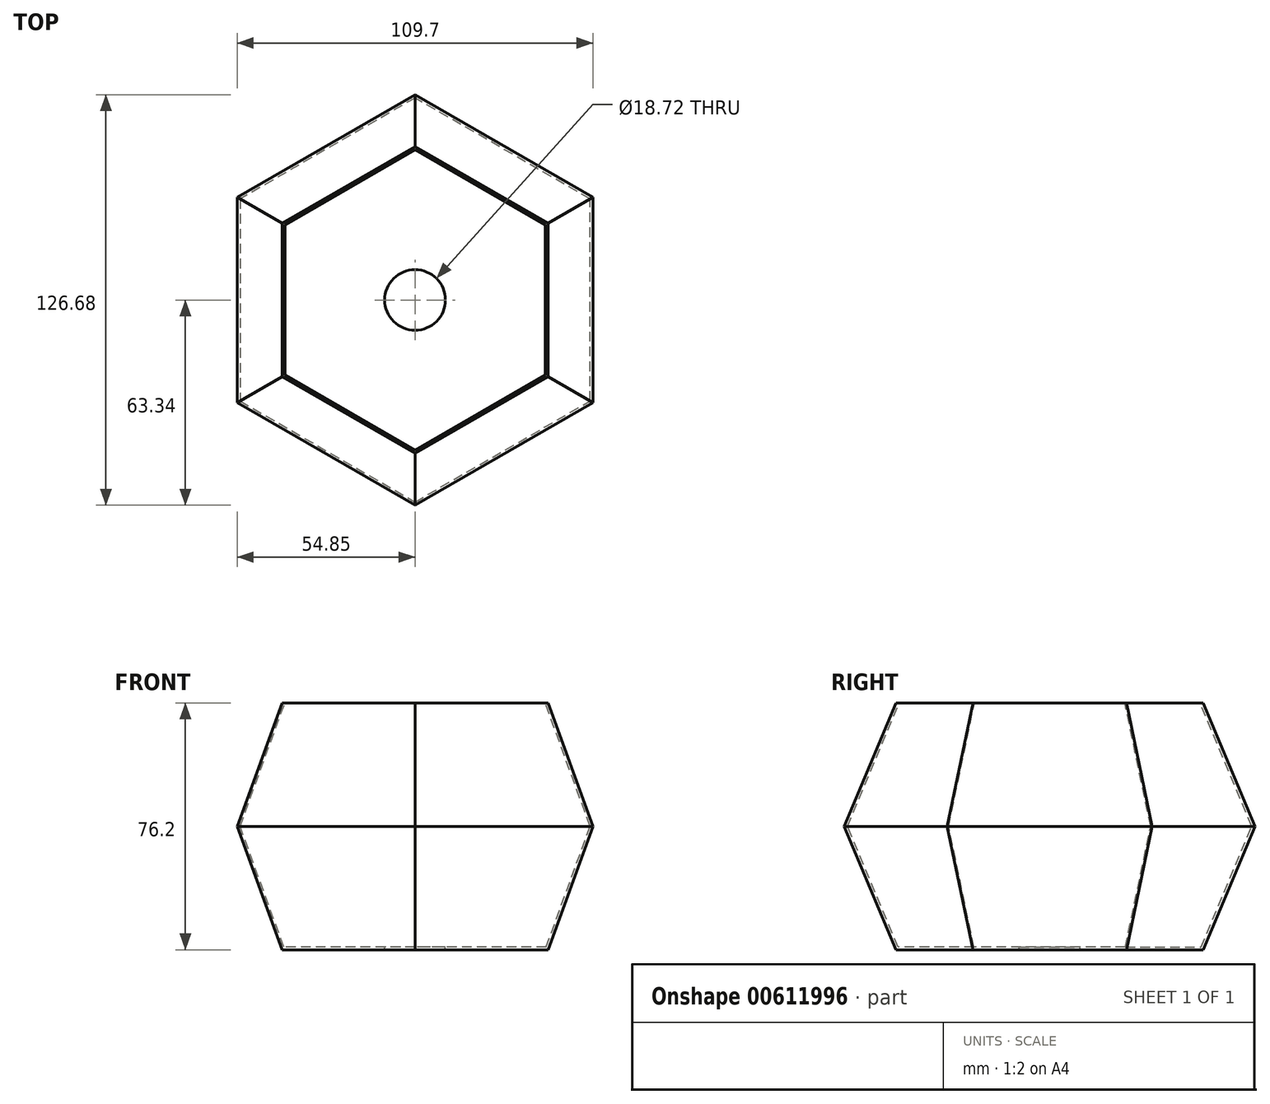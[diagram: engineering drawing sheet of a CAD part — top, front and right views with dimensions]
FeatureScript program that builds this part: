
annotation { "Feature Type Name" : "Feature", "Feature Type Description" : "" }
export const myFeature = defineFeature(function(context is Context, id is Id, definition is map)
    precondition{}
    {
        {
            var Q0;
            Q0=qCreatedBy(makeId("Top.planeOp"),FACE);
            var sketch = newSketch(context, id + "F0", { "sketchPlane" : qUnion([Q0])});
            skCircle(sketch, "E0.cCircle", {"center": v(0, 0) * mm, "radius": 41.01 * mm, "construction": true});
            skLineSegment(sketch, "E0.0", {"start": v(41.01, 23.68) * mm, "end": v(41.01, -23.68) * mm});
            skLineSegment(sketch, "E0.1", {"start": v(41.01, -23.68) * mm, "end": v(0, -47.36) * mm});
            skLineSegment(sketch, "E0.2", {"start": v(0, -47.36) * mm, "end": v(-41.01, -23.68) * mm});
            skLineSegment(sketch, "E0.3", {"start": v(-41.01, -23.68) * mm, "end": v(-41.01, 23.68) * mm});
            skLineSegment(sketch, "E0.4", {"start": v(-41.01, 23.68) * mm, "end": v(0, 47.36) * mm});
            skLineSegment(sketch, "E0.5", {"start": v(0, 47.36) * mm, "end": v(41.01, 23.68) * mm});
            skPoint(sketch, "E0.0.midPoint", {"position": v(41.01, 0) * mm});
            skSolve(sketch);
        }
        {
            var Q0;
            Q0=qCreatedBy(makeId("Top.planeOp"),FACE);
            cPlane(context, id + "F1", {"entities" : qUnion([Q0]), "cplaneType" : CPlaneType.OFFSET, "offset" : 38.1 * mm, "width" : 152.4 * mm, "height" : 152.4 * mm});
        }
        {
            var Q0;
            Q0=qCreatedBy(id+"F1.planeOp",FACE);
            var sketch = newSketch(context, id + "F2", { "sketchPlane" : qUnion([Q0])});
            skCircle(sketch, "E1.cCircle", {"center": v(0, 0) * mm, "radius": 54.85 * mm, "construction": true});
            skLineSegment(sketch, "E1.0", {"start": v(54.85, 31.67) * mm, "end": v(54.85, -31.67) * mm});
            skLineSegment(sketch, "E1.1", {"start": v(54.85, -31.67) * mm, "end": v(0, -63.34) * mm});
            skLineSegment(sketch, "E1.2", {"start": v(0, -63.34) * mm, "end": v(-54.85, -31.67) * mm});
            skLineSegment(sketch, "E1.3", {"start": v(-54.85, -31.67) * mm, "end": v(-54.85, 31.67) * mm});
            skLineSegment(sketch, "E1.4", {"start": v(-54.85, 31.67) * mm, "end": v(0, 63.34) * mm});
            skLineSegment(sketch, "E1.5", {"start": v(0, 63.34) * mm, "end": v(54.85, 31.67) * mm});
            skPoint(sketch, "E1.0.midPoint", {"position": v(54.85, 0) * mm});
            skSolve(sketch);
        }
        {
            var Q0;
            Q0=makeQuery(id+"F0.imprint","IMPRINT",FACE,{"disambiguationData":[TD([[makeQuery(id+"F0.imprint","IMPRINT",EDGE,{"derivedFrom":sQuery(id+"F0.wireOp",EDGE,"E0.0")}),-1.0]])]});
            var Q1;
            Q1=makeQuery(id+"F2.imprint","IMPRINT",FACE,{"disambiguationData":[TD([[makeQuery(id+"F2.imprint","IMPRINT",EDGE,{"derivedFrom":sQuery(id+"F2.wireOp",EDGE,"E1.0")}),-1.0]])]});
            loft(context, id + "F3", {"sheetProfilesArray" : [{ "sheetProfileEntities" : qUnion([Q0]) }, { "sheetProfileEntities" : qUnion([Q1]) }]});
        }
        {
            var Q0;
            Q0=qCreatedBy(id+"F1.planeOp",FACE);
            cPlane(context, id + "F4", {"entities" : qUnion([Q0]), "cplaneType" : CPlaneType.OFFSET, "offset" : 38.1 * mm, "width" : 152.4 * mm, "height" : 152.4 * mm});
        }
        {
            var Q0;
            Q0=qCreatedBy(id+"F4.planeOp",FACE);
            var sketch = newSketch(context, id + "F5", { "sketchPlane" : qUnion([Q0])});
            skLineSegment(sketch, "E2.0.0", {"start": v(41.01, 23.68) * mm, "end": v(0, 47.36) * mm});
            skLineSegment(sketch, "E2.0.1", {"start": v(41.01, -23.68) * mm, "end": v(41.01, 23.68) * mm});
            skLineSegment(sketch, "E2.0.2", {"start": v(0, -47.36) * mm, "end": v(41.01, -23.68) * mm});
            skLineSegment(sketch, "E2.0.3", {"start": v(-41.01, -23.68) * mm, "end": v(0, -47.36) * mm});
            skLineSegment(sketch, "E2.0.4", {"start": v(-41.01, 23.68) * mm, "end": v(-41.01, -23.68) * mm});
            skLineSegment(sketch, "E2.0.5", {"start": v(0, 47.36) * mm, "end": v(-41.01, 23.68) * mm});
            skSolve(sketch);
        }
        {
            var Q1;
            Q1 = qSketchRegion(id + "F2", true);
            var Q2;
            Q2 = qSketchRegion(id + "F5", true);
            loft(context, id + "F6", {"operationType" : NewBodyOperationType.ADD, "sheetProfilesArray" : [{ "sheetProfileEntities" : qUnion([Q1]) }, { "sheetProfileEntities" : qUnion([Q2]) }]});
        }
        {
            var Q0;
            Q0=makeQuery(id+"F6.opLoft","CAP_FACE",FACE,{"disambiguationData":[OSD([makeQuery(id+"F5.imprint","IMPRINT",FACE,{"disambiguationData":[TD([[makeQuery(id+"F5.imprint","IMPRINT",EDGE,{"derivedFrom":sQuery(id+"F5.wireOp",EDGE,"E2.0.0")}),1.0]])]})])],"isStart":true});
            shell(context, id + "F7", {"entities" : qUnion([Q0]), "thickness" : .8 * mm});
        }
        {
            var Q0;
            Q0=makeQuery(id+"F7.opShell","OFFSET_FACE",FACE,{"disambiguationData":[OSD([makeQuery(id+"F0.imprint","IMPRINT",FACE,{"disambiguationData":[TD([[makeQuery(id+"F0.imprint","IMPRINT",EDGE,{"derivedFrom":sQuery(id+"F0.wireOp",EDGE,"E0.0")}),-1.0]])]})])]});
            var sketch = newSketch(context, id + "F8", { "sketchPlane" : qUnion([Q0])});
            skCircle(sketch, "E3", {"center": v(0, 0) * mm, "radius": 9.36 * mm});
            skSolve(sketch);
        }
        {
            var Q0;
            Q0 = qSketchRegion(id + "F8", true);
            extrude(context, id + "F9", {"entities" : qUnion([Q0]), "operationType" : NewBodyOperationType.REMOVE, "endBound" : BoundingType.THROUGH_ALL, "oppositeDirection" : true, "depth" : 25.4 * mm, "offsetDistance" : 25.4 * mm});
        }
    });
